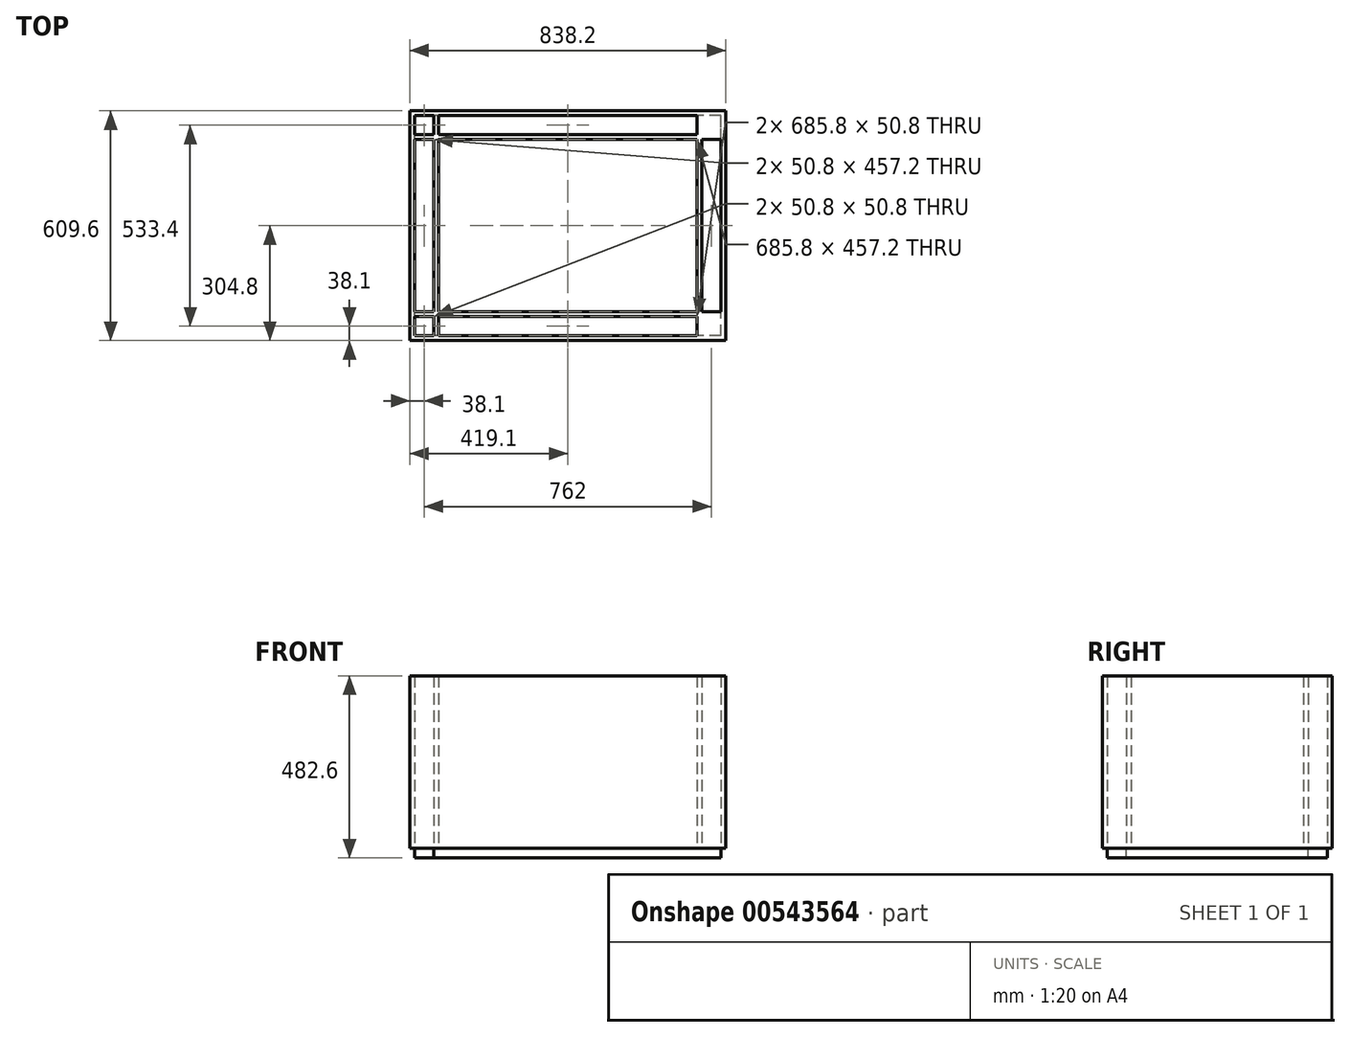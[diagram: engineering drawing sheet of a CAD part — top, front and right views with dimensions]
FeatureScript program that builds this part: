
annotation { "Feature Type Name" : "Feature", "Feature Type Description" : "" }
export const myFeature = defineFeature(function(context is Context, id is Id, definition is map)
    precondition{}
    {
        {
            var Q0;
            Q0=qCreatedBy(makeId("Top.planeOp"),FACE);
            var sketch = newSketch(context, id + "F0", { "sketchPlane" : qUnion([Q0])});
            skLineSegment(sketch, "E0.bottom", {"start": v(355.6, -241.3) * mm, "end": v(-355.6, -241.3) * mm});
            skLineSegment(sketch, "E0.top", {"start": v(355.6, 241.3) * mm, "end": v(-355.6, 241.3) * mm});
            skLineSegment(sketch, "E0.left", {"start": v(355.6, -241.3) * mm, "end": v(355.6, 241.3) * mm});
            skLineSegment(sketch, "E0.right", {"start": v(-355.6, -241.3) * mm, "end": v(-355.6, 241.3) * mm});
            skPoint(sketch, "E0.middle", {"position": v(0, 0) * mm});
            skLineSegment(sketch, "E1.bottom", {"start": v(406.4, -292.1) * mm, "end": v(-406.4, -292.1) * mm});
            skLineSegment(sketch, "E1.top", {"start": v(406.4, 292.1) * mm, "end": v(-406.4, 292.1) * mm});
            skLineSegment(sketch, "E1.left", {"start": v(406.4, -292.1) * mm, "end": v(406.4, 292.1) * mm});
            skLineSegment(sketch, "E1.right", {"start": v(-406.4, -292.1) * mm, "end": v(-406.4, 292.1) * mm});
            skLineSegment(sketch, "E2.bottom", {"start": v(355.6, -241.3) * mm, "end": v(406.4, -241.3) * mm});
            skLineSegment(sketch, "E2.top", {"start": v(355.6, -292.1) * mm, "end": v(406.4, -292.1) * mm});
            skLineSegment(sketch, "E2.left", {"start": v(355.6, -241.3) * mm, "end": v(355.6, -292.1) * mm});
            skLineSegment(sketch, "E2.right", {"start": v(406.4, -241.3) * mm, "end": v(406.4, -292.1) * mm});
            skLineSegment(sketch, "E3.bottom", {"start": v(355.6, 241.3) * mm, "end": v(406.4, 241.3) * mm});
            skLineSegment(sketch, "E3.top", {"start": v(355.6, 292.1) * mm, "end": v(406.4, 292.1) * mm});
            skLineSegment(sketch, "E3.left", {"start": v(355.6, 241.3) * mm, "end": v(355.6, 292.1) * mm});
            skLineSegment(sketch, "E3.right", {"start": v(406.4, 241.3) * mm, "end": v(406.4, 292.1) * mm});
            skLineSegment(sketch, "E4.bottom", {"start": v(-406.4, 292.1) * mm, "end": v(-355.6, 292.1) * mm});
            skLineSegment(sketch, "E4.top", {"start": v(-406.4, 241.3) * mm, "end": v(-355.6, 241.3) * mm});
            skLineSegment(sketch, "E4.left", {"start": v(-406.4, 292.1) * mm, "end": v(-406.4, 241.3) * mm});
            skLineSegment(sketch, "E4.right", {"start": v(-355.6, 292.1) * mm, "end": v(-355.6, 241.3) * mm});
            skLineSegment(sketch, "E5.bottom", {"start": v(-406.4, -292.1) * mm, "end": v(-355.6, -292.1) * mm});
            skLineSegment(sketch, "E5.top", {"start": v(-406.4, -241.3) * mm, "end": v(-355.6, -241.3) * mm});
            skLineSegment(sketch, "E5.left", {"start": v(-406.4, -292.1) * mm, "end": v(-406.4, -241.3) * mm});
            skLineSegment(sketch, "E5.right", {"start": v(-355.6, -292.1) * mm, "end": v(-355.6, -241.3) * mm});
            skLineSegment(sketch, "E6.bottom", {"start": v(342.9, -228.6) * mm, "end": v(-342.9, -228.6) * mm});
            skLineSegment(sketch, "E6.top", {"start": v(342.9, 228.6) * mm, "end": v(-342.9, 228.6) * mm});
            skLineSegment(sketch, "E6.left", {"start": v(342.9, -228.6) * mm, "end": v(342.9, 228.6) * mm});
            skLineSegment(sketch, "E6.right", {"start": v(-342.9, -228.6) * mm, "end": v(-342.9, 228.6) * mm});
            skLineSegment(sketch, "E7.bottom", {"start": v(419.1, -304.8) * mm, "end": v(-419.1, -304.8) * mm});
            skLineSegment(sketch, "E7.top", {"start": v(419.1, 304.8) * mm, "end": v(-419.1, 304.8) * mm});
            skLineSegment(sketch, "E7.left", {"start": v(419.1, -304.8) * mm, "end": v(419.1, 304.8) * mm});
            skLineSegment(sketch, "E7.right", {"start": v(-419.1, -304.8) * mm, "end": v(-419.1, 304.8) * mm});
            skLineSegment(sketch, "E8", {"start": v(-342.9, -228.6) * mm, "end": v(-342.9, -292.1) * mm});
            skLineSegment(sketch, "E9", {"start": v(-342.9, -228.6) * mm, "end": v(-406.4, -228.6) * mm});
            skLineSegment(sketch, "E10", {"start": v(342.9, -228.6) * mm, "end": v(342.9, -292.1) * mm});
            skLineSegment(sketch, "E11", {"start": v(342.9, -228.6) * mm, "end": v(406.4, -228.6) * mm});
            skLineSegment(sketch, "E12", {"start": v(342.9, 228.6) * mm, "end": v(406.4, 228.6) * mm});
            skLineSegment(sketch, "E13", {"start": v(342.9, 228.6) * mm, "end": v(342.9, 292.1) * mm});
            skLineSegment(sketch, "E14", {"start": v(-342.9, 228.6) * mm, "end": v(-342.9, 292.1) * mm});
            skLineSegment(sketch, "E15", {"start": v(-342.9, 228.6) * mm, "end": v(-406.4, 228.6) * mm});
            skSolve(sketch);
        }
        {
            var Q0;
            Q0=makeQuery(id+"F0.imprint","IMPRINT",FACE,{"disambiguationData":[TD([[makeQuery(id+"F0.imprint","IMPRINT",EDGE,{"derivedFrom":sQuery(id+"F0.wireOp",EDGE,"E0.bottom")}),-1.0]])]});
            var Q1;
            Q1=makeQuery(id+"F0.imprint","IMPRINT",FACE,{"disambiguationData":[TD([[makeQuery(id+"F0.imprint","IMPRINT",EDGE,{"derivedFrom":sQuery(id+"F0.wireOp",EDGE,"E4.bottom")}),-1.0]])]});
            var Q2;
            Q2=makeQuery(id+"F0.imprint","IMPRINT",FACE,{"disambiguationData":[TD([[makeQuery(id+"F0.imprint","IMPRINT",EDGE,{"derivedFrom":sQuery(id+"F0.wireOp",EDGE,"E3.bottom")}),1.0]])]});
            var Q3;
            Q3=makeQuery(id+"F0.imprint","IMPRINT",FACE,{"disambiguationData":[TD([[makeQuery(id+"F0.imprint","IMPRINT",EDGE,{"derivedFrom":sQuery(id+"F0.wireOp",EDGE,"E2.bottom")}),-1.0]])]});
            var Q4;
            Q4=makeQuery(id+"F0.imprint","IMPRINT",FACE,{"disambiguationData":[TD([[makeQuery(id+"F0.imprint","IMPRINT",EDGE,{"derivedFrom":sQuery(id+"F0.wireOp",EDGE,"E5.bottom")}),1.0]])]});
            var Q5;
            Q5=makeQuery(id+"F0.imprint","IMPRINT",FACE,{"disambiguationData":[TD([[makeQuery(id+"F0.imprint","IMPRINT",EDGE,{"derivedFrom":sQuery(id+"F0.wireOp",EDGE,"E1.bottom")}),1.0]])]});
            var Q6;
            {var subQ0=sQuery(id+"F0.wireOp",EDGE,"E4.top");Q6=makeQuery(id+"F0.imprint","IMPRINT",FACE,{"disambiguationData":[TD([[makeQuery(id+"F0.imprint","IMPRINT",EDGE,{"derivedFrom":subQ0}),-1.0]])]});}
            var Q7;
            {var subQ1=sQuery(id+"F0.wireOp",EDGE,"E0.top");var subQ3=sQuery(id+"F0.wireOp",EDGE,"E14");var subQ4=makeQuery(id+"F0.imprint","INTERSECT",VERTEX,{"derivedFrom":[subQ1,subQ3]});Q7=makeQuery(id+"F0.imprint","IMPRINT",FACE,{"disambiguationData":[TD([[makeQuery(id+"F0.imprint","IMPRINT",EDGE,{"disambiguationData":[TD([[subQ4,-1.0]])],"derivedFrom":subQ1}),1.0]])]});}
            var Q8;
            {var subQ0=sQuery(id+"F0.wireOp",EDGE,"E4.right");Q8=makeQuery(id+"F0.imprint","IMPRINT",FACE,{"disambiguationData":[TD([[makeQuery(id+"F0.imprint","IMPRINT",EDGE,{"derivedFrom":subQ0}),1.0]])]});}
            var Q9;
            {var subQ5=sQuery(id+"F0.wireOp",EDGE,"E6.top");Q9=makeQuery(id+"F0.imprint","IMPRINT",FACE,{"disambiguationData":[TD([[makeQuery(id+"F0.imprint","IMPRINT",EDGE,{"derivedFrom":subQ5}),-1.0]])]});}
            var Q10;
            {var subQ5=sQuery(id+"F0.wireOp",EDGE,"E6.right");Q10=makeQuery(id+"F0.imprint","IMPRINT",FACE,{"disambiguationData":[TD([[makeQuery(id+"F0.imprint","IMPRINT",EDGE,{"derivedFrom":subQ5}),1.0]])]});}
            var Q11;
            {var subQ5=sQuery(id+"F0.wireOp",EDGE,"E6.left");Q11=makeQuery(id+"F0.imprint","IMPRINT",FACE,{"disambiguationData":[TD([[makeQuery(id+"F0.imprint","IMPRINT",EDGE,{"derivedFrom":subQ5}),-1.0]])]});}
            var Q12;
            {var subQ0=sQuery(id+"F0.wireOp",EDGE,"E3.left");Q12=makeQuery(id+"F0.imprint","IMPRINT",FACE,{"disambiguationData":[TD([[makeQuery(id+"F0.imprint","IMPRINT",EDGE,{"derivedFrom":subQ0}),1.0]])]});}
            var Q13;
            {var subQ1=sQuery(id+"F0.wireOp",EDGE,"E0.top");var subQ3=sQuery(id+"F0.wireOp",EDGE,"E13");var subQ4=makeQuery(id+"F0.imprint","INTERSECT",VERTEX,{"derivedFrom":[subQ1,subQ3]});Q13=makeQuery(id+"F0.imprint","IMPRINT",FACE,{"disambiguationData":[TD([[makeQuery(id+"F0.imprint","IMPRINT",EDGE,{"disambiguationData":[TD([[subQ4,1.0]])],"derivedFrom":subQ1}),1.0]])]});}
            var Q14;
            {var subQ0=sQuery(id+"F0.wireOp",EDGE,"E3.bottom");Q14=makeQuery(id+"F0.imprint","IMPRINT",FACE,{"disambiguationData":[TD([[makeQuery(id+"F0.imprint","IMPRINT",EDGE,{"derivedFrom":subQ0}),-1.0]])]});}
            var Q15;
            {var subQ0=sQuery(id+"F0.wireOp",EDGE,"E2.left");Q15=makeQuery(id+"F0.imprint","IMPRINT",FACE,{"disambiguationData":[TD([[makeQuery(id+"F0.imprint","IMPRINT",EDGE,{"derivedFrom":subQ0}),-1.0]])]});}
            var Q16;
            {var subQ0=sQuery(id+"F0.wireOp",EDGE,"E2.bottom");Q16=makeQuery(id+"F0.imprint","IMPRINT",FACE,{"disambiguationData":[TD([[makeQuery(id+"F0.imprint","IMPRINT",EDGE,{"derivedFrom":subQ0}),1.0]])]});}
            var Q17;
            {var subQ0=sQuery(id+"F0.wireOp",EDGE,"E5.top");Q17=makeQuery(id+"F0.imprint","IMPRINT",FACE,{"disambiguationData":[TD([[makeQuery(id+"F0.imprint","IMPRINT",EDGE,{"derivedFrom":subQ0}),1.0]])]});}
            var Q18;
            {var subQ0=sQuery(id+"F0.wireOp",EDGE,"E5.right");Q18=makeQuery(id+"F0.imprint","IMPRINT",FACE,{"disambiguationData":[TD([[makeQuery(id+"F0.imprint","IMPRINT",EDGE,{"derivedFrom":subQ0}),-1.0]])]});}
            extrude(context, id + "F1", {"entities" : qUnion([Q0, Q1, Q2, Q3, Q4, Q5, Q6, Q7, Q8, Q9, Q10, Q11, Q12, Q13, Q14, Q15, Q16, Q17, Q18]), "depth" : 457.2 * mm, "offsetDistance" : 25.4 * mm});
        }
        {
            var Q0;
            {var subQ0=sQuery(id+"F0.wireOp",EDGE,"E11");var subQ1=sQuery(id+"F0.wireOp",EDGE,"E0.left");var subQ2=makeQuery(id+"F0.imprint","INTERSECT",VERTEX,{"derivedFrom":[subQ1,subQ0]});Q0=makeQuery(id+"F0.imprint","IMPRINT",FACE,{"disambiguationData":[TD([[makeQuery(id+"F0.imprint","IMPRINT",EDGE,{"disambiguationData":[TD([[subQ2,-1.0]])],"derivedFrom":subQ1}),-1.0]])]});}
            var Q1;
            {var subQ0=sQuery(id+"F0.wireOp",EDGE,"E4.top");Q1=makeQuery(id+"F0.imprint","IMPRINT",FACE,{"disambiguationData":[TD([[makeQuery(id+"F0.imprint","IMPRINT",EDGE,{"derivedFrom":subQ0}),-1.0]])]});}
            var Q2;
            {var subQ0=sQuery(id+"F0.wireOp",EDGE,"E3.bottom");Q2=makeQuery(id+"F0.imprint","IMPRINT",FACE,{"disambiguationData":[TD([[makeQuery(id+"F0.imprint","IMPRINT",EDGE,{"derivedFrom":subQ0}),-1.0]])]});}
            var Q3;
            {var subQ5=sQuery(id+"F0.wireOp",EDGE,"E6.bottom");Q3=makeQuery(id+"F0.imprint","IMPRINT",FACE,{"disambiguationData":[TD([[makeQuery(id+"F0.imprint","IMPRINT",EDGE,{"derivedFrom":subQ5}),1.0]])]});}
            var Q4;
            Q4=makeQuery(id+"F0.imprint","IMPRINT",FACE,{"disambiguationData":[TD([[makeQuery(id+"F0.imprint","IMPRINT",EDGE,{"derivedFrom":sQuery(id+"F0.wireOp",EDGE,"E4.bottom")}),-1.0]])]});
            var Q5;
            Q5=makeQuery(id+"F0.imprint","IMPRINT",FACE,{"disambiguationData":[TD([[makeQuery(id+"F0.imprint","IMPRINT",EDGE,{"derivedFrom":sQuery(id+"F0.wireOp",EDGE,"E6.bottom")}),-1.0]])]});
            var Q6;
            {var subQ5=sQuery(id+"F0.wireOp",EDGE,"E6.right");Q6=makeQuery(id+"F0.imprint","IMPRINT",FACE,{"disambiguationData":[TD([[makeQuery(id+"F0.imprint","IMPRINT",EDGE,{"derivedFrom":subQ5}),1.0]])]});}
            var Q7;
            {var subQ5=sQuery(id+"F0.wireOp",EDGE,"E6.top");Q7=makeQuery(id+"F0.imprint","IMPRINT",FACE,{"disambiguationData":[TD([[makeQuery(id+"F0.imprint","IMPRINT",EDGE,{"derivedFrom":subQ5}),-1.0]])]});}
            var Q8;
            {var subQ0=sQuery(id+"F0.wireOp",EDGE,"E13");var subQ1=sQuery(id+"F0.wireOp",EDGE,"E0.top");var subQ2=makeQuery(id+"F0.imprint","INTERSECT",VERTEX,{"derivedFrom":[subQ1,subQ0]});Q8=makeQuery(id+"F0.imprint","IMPRINT",FACE,{"disambiguationData":[TD([[makeQuery(id+"F0.imprint","IMPRINT",EDGE,{"disambiguationData":[TD([[subQ2,-1.0]])],"derivedFrom":subQ1}),-1.0]])]});}
            var Q9;
            {var subQ0=sQuery(id+"F0.wireOp",EDGE,"E9");var subQ1=sQuery(id+"F0.wireOp",EDGE,"E0.right");var subQ2=makeQuery(id+"F0.imprint","INTERSECT",VERTEX,{"derivedFrom":[subQ1,subQ0]});Q9=makeQuery(id+"F0.imprint","IMPRINT",FACE,{"disambiguationData":[TD([[makeQuery(id+"F0.imprint","IMPRINT",EDGE,{"disambiguationData":[TD([[subQ2,-1.0]])],"derivedFrom":subQ1}),1.0]])]});}
            var Q10;
            {var subQ0=sQuery(id+"F0.wireOp",EDGE,"E5.top");Q10=makeQuery(id+"F0.imprint","IMPRINT",FACE,{"disambiguationData":[TD([[makeQuery(id+"F0.imprint","IMPRINT",EDGE,{"derivedFrom":subQ0}),1.0]])]});}
            var Q11;
            {var subQ0=sQuery(id+"F0.wireOp",EDGE,"E4.right");Q11=makeQuery(id+"F0.imprint","IMPRINT",FACE,{"disambiguationData":[TD([[makeQuery(id+"F0.imprint","IMPRINT",EDGE,{"derivedFrom":subQ0}),1.0]])]});}
            var Q12;
            {var subQ0=sQuery(id+"F0.wireOp",EDGE,"E2.bottom");Q12=makeQuery(id+"F0.imprint","IMPRINT",FACE,{"disambiguationData":[TD([[makeQuery(id+"F0.imprint","IMPRINT",EDGE,{"derivedFrom":subQ0}),1.0]])]});}
            var Q13;
            Q13=makeQuery(id+"F0.imprint","IMPRINT",FACE,{"disambiguationData":[TD([[makeQuery(id+"F0.imprint","IMPRINT",EDGE,{"derivedFrom":sQuery(id+"F0.wireOp",EDGE,"E2.bottom")}),-1.0]])]});
            var Q14;
            Q14=makeQuery(id+"F0.imprint","IMPRINT",FACE,{"disambiguationData":[TD([[makeQuery(id+"F0.imprint","IMPRINT",EDGE,{"derivedFrom":sQuery(id+"F0.wireOp",EDGE,"E3.bottom")}),1.0]])]});
            var Q15;
            Q15=makeQuery(id+"F0.imprint","IMPRINT",FACE,{"disambiguationData":[TD([[makeQuery(id+"F0.imprint","IMPRINT",EDGE,{"derivedFrom":sQuery(id+"F0.wireOp",EDGE,"E5.bottom")}),1.0]])]});
            var Q16;
            {var subQ0=sQuery(id+"F0.wireOp",EDGE,"E2.left");Q16=makeQuery(id+"F0.imprint","IMPRINT",FACE,{"disambiguationData":[TD([[makeQuery(id+"F0.imprint","IMPRINT",EDGE,{"derivedFrom":subQ0}),-1.0]])]});}
            var Q17;
            {var subQ0=sQuery(id+"F0.wireOp",EDGE,"E5.right");Q17=makeQuery(id+"F0.imprint","IMPRINT",FACE,{"disambiguationData":[TD([[makeQuery(id+"F0.imprint","IMPRINT",EDGE,{"derivedFrom":subQ0}),-1.0]])]});}
            var Q18;
            {var subQ0=sQuery(id+"F0.wireOp",EDGE,"E10");var subQ1=sQuery(id+"F0.wireOp",EDGE,"E0.bottom");var subQ2=makeQuery(id+"F0.imprint","INTERSECT",VERTEX,{"derivedFrom":[subQ1,subQ0]});Q18=makeQuery(id+"F0.imprint","IMPRINT",FACE,{"disambiguationData":[TD([[makeQuery(id+"F0.imprint","IMPRINT",EDGE,{"disambiguationData":[TD([[subQ2,-1.0]])],"derivedFrom":subQ1}),1.0]])]});}
            var Q19;
            {var subQ0=sQuery(id+"F0.wireOp",EDGE,"E3.left");Q19=makeQuery(id+"F0.imprint","IMPRINT",FACE,{"disambiguationData":[TD([[makeQuery(id+"F0.imprint","IMPRINT",EDGE,{"derivedFrom":subQ0}),1.0]])]});}
            var Q20;
            {var subQ5=sQuery(id+"F0.wireOp",EDGE,"E6.left");Q20=makeQuery(id+"F0.imprint","IMPRINT",FACE,{"disambiguationData":[TD([[makeQuery(id+"F0.imprint","IMPRINT",EDGE,{"derivedFrom":subQ5}),-1.0]])]});}
            var Q21;
            {var subQ5=sQuery(id+"F0.wireOp",EDGE,"E2.top");Q21=makeQuery(id+"F0.imprint","IMPRINT",FACE,{"disambiguationData":[TD([[makeQuery(id+"F0.imprint","IMPRINT",EDGE,{"derivedFrom":subQ5}),-1.0]])]});}
            var Q22;
            {var subQ1=sQuery(id+"F0.wireOp",EDGE,"E0.bottom");var subQ3=sQuery(id+"F0.wireOp",EDGE,"E8");var subQ4=makeQuery(id+"F0.imprint","INTERSECT",VERTEX,{"derivedFrom":[subQ1,subQ3]});Q22=makeQuery(id+"F0.imprint","IMPRINT",FACE,{"disambiguationData":[TD([[makeQuery(id+"F0.imprint","IMPRINT",EDGE,{"disambiguationData":[TD([[subQ4,-1.0]])],"derivedFrom":subQ1}),-1.0]])]});}
            var Q23;
            {var subQ1=sQuery(id+"F0.wireOp",EDGE,"E0.top");var subQ3=sQuery(id+"F0.wireOp",EDGE,"E13");var subQ4=makeQuery(id+"F0.imprint","INTERSECT",VERTEX,{"derivedFrom":[subQ1,subQ3]});Q23=makeQuery(id+"F0.imprint","IMPRINT",FACE,{"disambiguationData":[TD([[makeQuery(id+"F0.imprint","IMPRINT",EDGE,{"disambiguationData":[TD([[subQ4,1.0]])],"derivedFrom":subQ1}),1.0]])]});}
            var Q24;
            {var subQ1=sQuery(id+"F0.wireOp",EDGE,"E0.top");var subQ3=sQuery(id+"F0.wireOp",EDGE,"E14");var subQ4=makeQuery(id+"F0.imprint","INTERSECT",VERTEX,{"derivedFrom":[subQ1,subQ3]});Q24=makeQuery(id+"F0.imprint","IMPRINT",FACE,{"disambiguationData":[TD([[makeQuery(id+"F0.imprint","IMPRINT",EDGE,{"disambiguationData":[TD([[subQ4,-1.0]])],"derivedFrom":subQ1}),1.0]])]});}
            var Q25;
            {var subQ1=sQuery(id+"F0.wireOp",EDGE,"E0.bottom");var subQ3=sQuery(id+"F0.wireOp",EDGE,"E10");var subQ4=makeQuery(id+"F0.imprint","INTERSECT",VERTEX,{"derivedFrom":[subQ1,subQ3]});Q25=makeQuery(id+"F0.imprint","IMPRINT",FACE,{"disambiguationData":[TD([[makeQuery(id+"F0.imprint","IMPRINT",EDGE,{"disambiguationData":[TD([[subQ4,1.0]])],"derivedFrom":subQ1}),-1.0]])]});}
            extrude(context, id + "F2", {"entities" : qUnion([Q0, Q1, Q2, Q3, Q4, Q5, Q6, Q7, Q8, Q9, Q10, Q11, Q12, Q13, Q14, Q15, Q16, Q17, Q18, Q19, Q20, Q21, Q22, Q23, Q24, Q25]), "oppositeDirection" : true, "depth" : 25.4 * mm, "offsetDistance" : 25.4 * mm});
        }
    });
